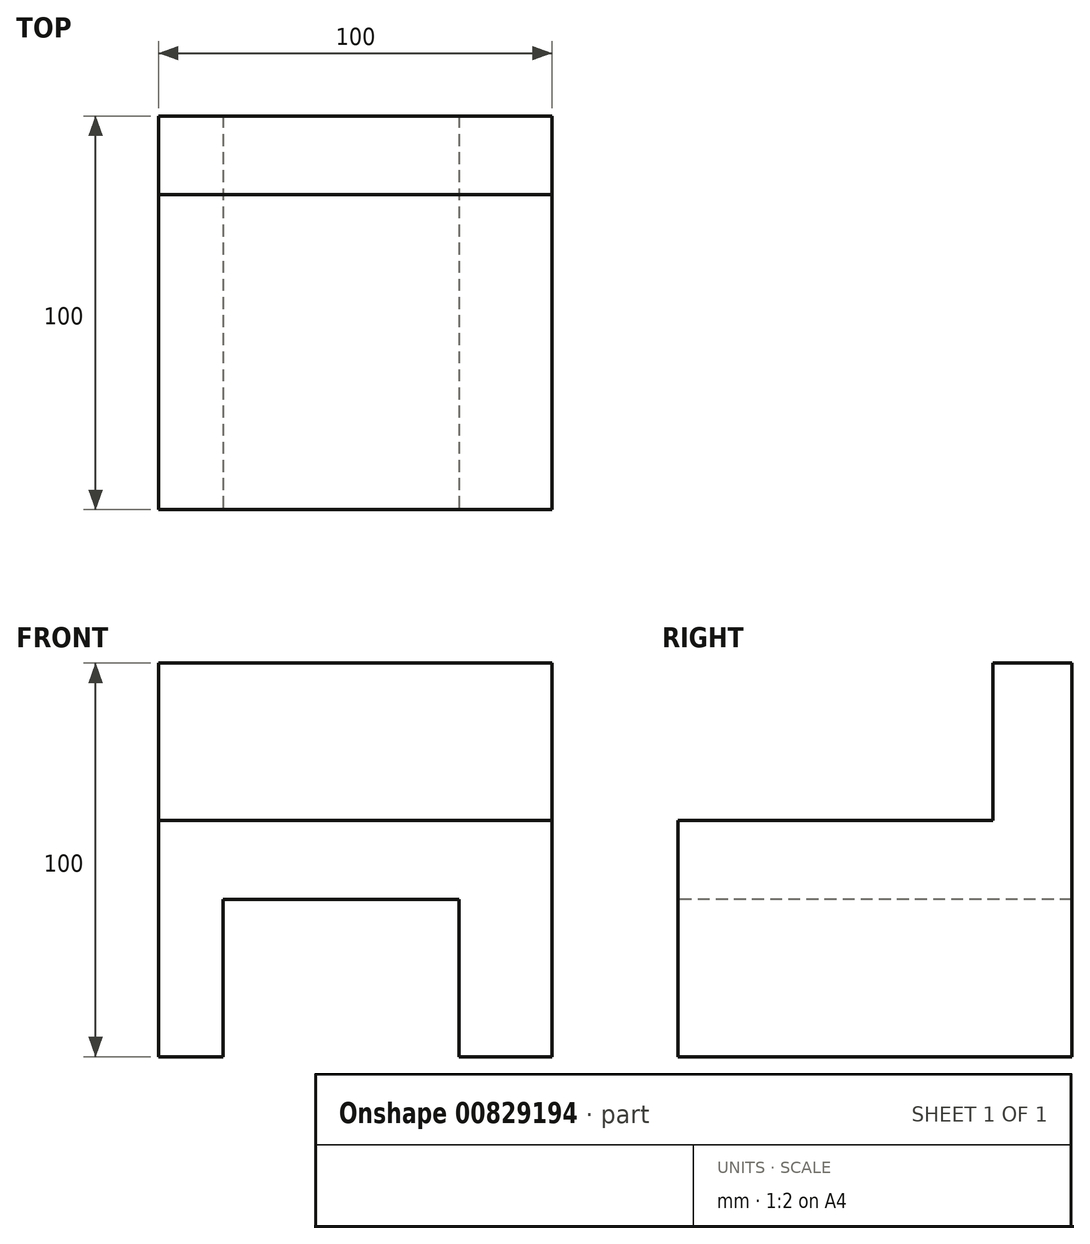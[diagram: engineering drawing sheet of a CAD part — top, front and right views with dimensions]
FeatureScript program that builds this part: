
annotation { "Feature Type Name" : "Feature", "Feature Type Description" : "" }
export const myFeature = defineFeature(function(context is Context, id is Id, definition is map)
    precondition{}
    {
        {
            var Q0;
            Q0=qCreatedBy(makeId("Top.planeOp"),FACE);
            var sketch = newSketch(context, id + "F0", { "sketchPlane" : qUnion([Q0])});
            skLineSegment(sketch, "E0.bottom", {"start": v(-50, 50) * mm, "end": v(50, 50) * mm});
            skLineSegment(sketch, "E0.top", {"start": v(-50, -50) * mm, "end": v(50, -50) * mm});
            skLineSegment(sketch, "E0.left", {"start": v(-50, 50) * mm, "end": v(-50, -50) * mm});
            skLineSegment(sketch, "E0.right", {"start": v(50, 50) * mm, "end": v(50, -50) * mm});
            skPoint(sketch, "E0.middle", {"position": v(0, 0) * mm});
            skSolve(sketch);
        }
        {
            var Q0;
            Q0 = qSketchRegion(id + "F0", true);
            extrude(context, id + "F1", {"entities" : qUnion([Q0]), "depth" : 100 * mm, "offsetDistance" : 25 * mm});
        }
        {
            var Q0;
            Q0=makeQuery(id+"F1.opExtrude","CAP_FACE",FACE,{"disambiguationData":[OSD([sQuery(id+"F0.wireOp",EDGE,"E0.bottom"),sQuery(id+"F0.wireOp",EDGE,"E0.top"),sQuery(id+"F0.wireOp",EDGE,"E0.left"),sQuery(id+"F0.wireOp",EDGE,"E0.right")])],"isStart":false});
            var sketch = newSketch(context, id + "F2", { "sketchPlane" : qUnion([Q0])});
            skLineSegment(sketch, "E1.bottom", {"start": v(-50, -50) * mm, "end": v(50, -50) * mm});
            skLineSegment(sketch, "E1.top", {"start": v(-50, 30) * mm, "end": v(50, 30) * mm});
            skLineSegment(sketch, "E1.left", {"start": v(-50, -50) * mm, "end": v(-50, 30) * mm});
            skLineSegment(sketch, "E1.right", {"start": v(50, -50) * mm, "end": v(50, 30) * mm});
            skSolve(sketch);
        }
        {
            var Q0;
            Q0=makeQuery(id+"F2.imprint","IMPRINT",FACE,{"disambiguationData":[TD([[makeQuery(id+"F2.imprint","IMPRINT",EDGE,{"derivedFrom":sQuery(id+"F2.wireOp",EDGE,"E1.bottom")}),1.0]])]});
            extrude(context, id + "F3", {"entities" : qUnion([Q0]), "operationType" : NewBodyOperationType.REMOVE, "oppositeDirection" : true, "depth" : 40 * mm, "offsetDistance" : 25 * mm});
        }
        {
            var Q0;
            Q0=makeQuery(id+"F1.opExtrude","SWEPT_FACE",FACE,{"disambiguationData":[OSD([sQuery(id+"F0.wireOp",EDGE,"E0.top")])]});
            var sketch = newSketch(context, id + "F4", { "sketchPlane" : qUnion([Q0])});
            skLineSegment(sketch, "E2.bottom", {"start": v(-33.61, 0) * mm, "end": v(26.39, 0) * mm});
            skLineSegment(sketch, "E2.top", {"start": v(-33.61, 40) * mm, "end": v(26.39, 40) * mm});
            skLineSegment(sketch, "E2.left", {"start": v(-33.61, 0) * mm, "end": v(-33.61, 40) * mm});
            skLineSegment(sketch, "E2.right", {"start": v(26.39, 0) * mm, "end": v(26.39, 40) * mm});
            skSolve(sketch);
        }
        {
            var Q0;
            Q0 = qSketchRegion(id + "F4", true);
            extrude(context, id + "F5", {"entities" : qUnion([Q0]), "operationType" : NewBodyOperationType.REMOVE, "endBound" : BoundingType.THROUGH_ALL, "oppositeDirection" : true, "depth" : 25 * mm, "offsetDistance" : 25 * mm});
        }
    });
